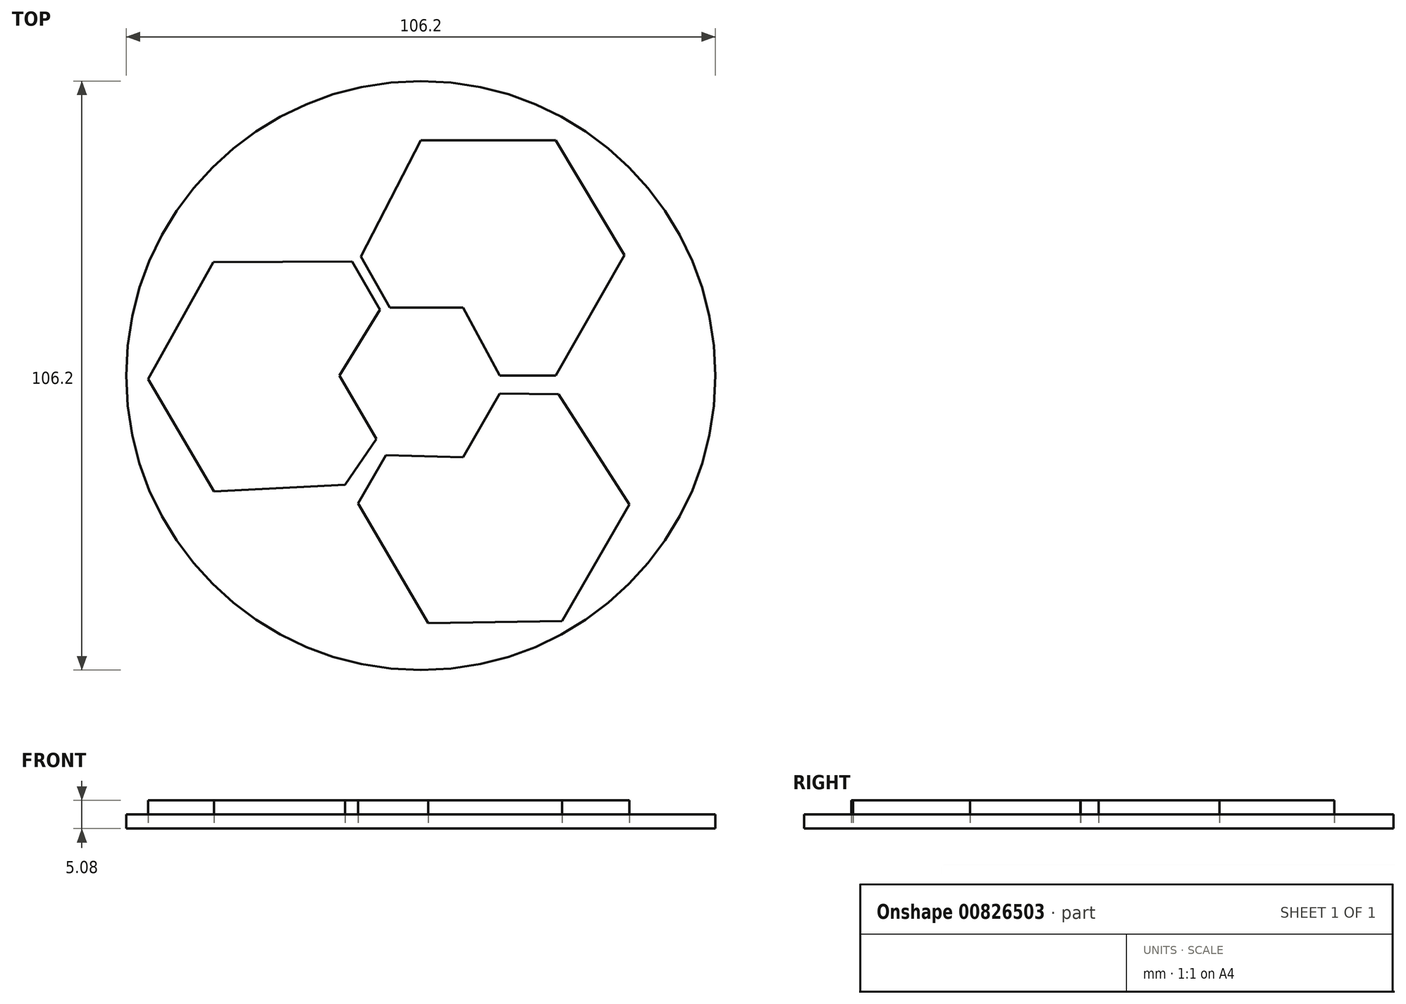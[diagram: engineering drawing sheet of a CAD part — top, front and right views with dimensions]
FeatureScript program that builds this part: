
annotation { "Feature Type Name" : "Feature", "Feature Type Description" : "" }
export const myFeature = defineFeature(function(context is Context, id is Id, definition is map)
    precondition{}
    {
        {
            var Q0;
            Q0=qCreatedBy(makeId("Top.planeOp"),FACE);
            var sketch = newSketch(context, id + "F0", { "sketchPlane" : qUnion([Q0])});
            skLineSegment(sketch, "E0", {"start": v(0, 42.45) * mm, "end": v(24.32, 42.45) * mm});
            skLineSegment(sketch, "E1", {"start": v(24.32, 42.45) * mm, "end": v(36.7, 21.73) * mm});
            skLineSegment(sketch, "E2", {"start": v(36.7, 21.73) * mm, "end": v(24.32, 0) * mm});
            skLineSegment(sketch, "E3", {"start": v(24.32, 0) * mm, "end": v(14.25, 0) * mm});
            skLineSegment(sketch, "E4", {"start": v(14.25, 0) * mm, "end": v(7.63, 12.23) * mm});
            skLineSegment(sketch, "E5", {"start": v(7.63, 12.23) * mm, "end": v(-5.61, 12.23) * mm});
            skLineSegment(sketch, "E6", {"start": v(-5.61, 12.23) * mm, "end": v(-10.8, 21.44) * mm});
            skLineSegment(sketch, "E7", {"start": v(0, 42.45) * mm, "end": v(-10.8, 21.44) * mm});
            skLineSegment(sketch, "E8", {"start": v(-37.27, -20.87) * mm, "end": v(-49.17, -0.64) * mm});
            skLineSegment(sketch, "E9", {"start": v(-49.17, -0.64) * mm, "end": v(-37.4, 20.44) * mm});
            skLineSegment(sketch, "E10", {"start": v(-37.4, 20.44) * mm, "end": v(-12.4, 20.58) * mm});
            skLineSegment(sketch, "E11", {"start": v(-12.4, 20.58) * mm, "end": v(-7.37, 11.86) * mm});
            skLineSegment(sketch, "E12", {"start": v(-7.37, 11.86) * mm, "end": v(-14.65, 0.01) * mm});
            skLineSegment(sketch, "E13", {"start": v(-14.65, 0.01) * mm, "end": v(-8.03, -11.45) * mm});
            skLineSegment(sketch, "E14", {"start": v(-8.03, -11.45) * mm, "end": v(-13.68, -19.7) * mm});
            skLineSegment(sketch, "E15", {"start": v(-37.27, -20.87) * mm, "end": v(-13.68, -19.7) * mm});
            skLineSegment(sketch, "E16", {"start": v(37.61, -23.2) * mm, "end": v(25.45, -44.27) * mm});
            skLineSegment(sketch, "E17", {"start": v(25.45, -44.27) * mm, "end": v(1.32, -44.63) * mm});
            skLineSegment(sketch, "E18", {"start": v(1.32, -44.63) * mm, "end": v(-11.31, -23.04) * mm});
            skLineSegment(sketch, "E19", {"start": v(-11.31, -23.04) * mm, "end": v(-6.27, -14.32) * mm});
            skLineSegment(sketch, "E20", {"start": v(-6.27, -14.32) * mm, "end": v(7.63, -14.7) * mm});
            skLineSegment(sketch, "E21", {"start": v(7.63, -14.7) * mm, "end": v(14.25, -3.24) * mm});
            skLineSegment(sketch, "E22", {"start": v(14.25, -3.24) * mm, "end": v(24.81, -3.36) * mm});
            skLineSegment(sketch, "E23", {"start": v(37.61, -23.2) * mm, "end": v(24.81, -3.36) * mm});
            skSolve(sketch);
        }
        {
            var Q0;
            Q0 = qSketchRegion(id + "F0", true);
            extrude(context, id + "F1", {"entities" : qUnion([Q0]), "depth" : 5.08 * mm, "offsetDistance" : 25.4 * mm});
        }
        {
            var Q0;
            Q0=qCreatedBy(makeId("Top.planeOp"),FACE);
            var sketch = newSketch(context, id + "F2", { "sketchPlane" : qUnion([Q0])});
            skCircle(sketch, "E24", {"center": v(0, 0) * mm, "radius": 53.1 * mm});
            skSolve(sketch);
        }
        {
            var Q0;
            Q0 = qSketchRegion(id + "F2", true);
            extrude(context, id + "F3", {"entities" : qUnion([Q0]), "depth" : 2.54 * mm, "offsetDistance" : 25.4 * mm});
        }
    });
